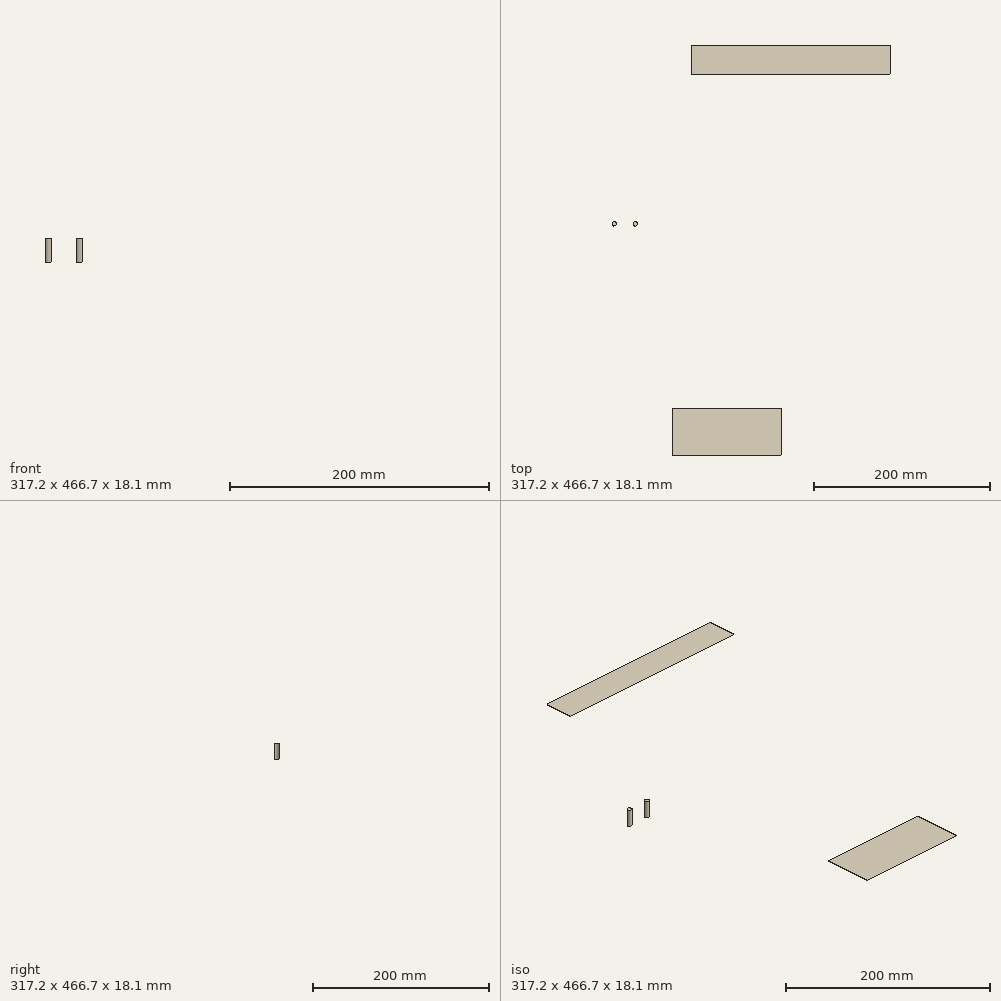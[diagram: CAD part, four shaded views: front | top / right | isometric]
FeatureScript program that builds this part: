
annotation { "Feature Type Name" : "Feature", "Feature Type Description" : "" }
export const myFeature = defineFeature(function(context is Context, id is Id, definition is map)
    precondition{}
    {
        {
            var Q0;
            Q0=qCreatedBy(makeId("Top.planeOp"),FACE);
            var sketch = newSketch(context, id + "F0", { "sketchPlane" : qUnion([Q0])});
            skLineSegment(sketch, "E0.bottom", {"start": v(0, 0) * mm, "end": v(500, 0) * mm});
            skLineSegment(sketch, "E0.top", {"start": v(0, 1000) * mm, "end": v(500, 1000) * mm});
            skLineSegment(sketch, "E0.left", {"start": v(0, 0) * mm, "end": v(0, 1000) * mm});
            skLineSegment(sketch, "E0.right", {"start": v(500, 0) * mm, "end": v(500, 1000) * mm});
            skSolve(sketch);
        }
        {
            var Q0;
            Q0=makeQuery(id+"F0.imprint","IMPRINT",FACE,{"disambiguationData":[TD([[makeQuery(id+"F0.imprint","IMPRINT",EDGE,{"derivedFrom":sQuery(id+"F0.wireOp",EDGE,"E0.bottom")}),1.0]])]});
            extrude(context, id + "F1", {"entities" : qUnion([Q0]), "depth" : 18 * mm, "offsetDistance" : 25 * mm});
        }
        {
            var Q0;
            Q0=makeQuery(id+"F1.opExtrude","CAP_FACE",FACE,{"disambiguationData":[OSD([sQuery(id+"F0.wireOp",EDGE,"E0.bottom"),sQuery(id+"F0.wireOp",EDGE,"E0.top"),sQuery(id+"F0.wireOp",EDGE,"E0.left"),sQuery(id+"F0.wireOp",EDGE,"E0.right")])],"isStart":false});
            var sketch = newSketch(context, id + "F2", { "sketchPlane" : qUnion([Q0])});
            skLineSegment(sketch, "E1", {"start": v(-62.28, 670) * mm, "end": v(483.72, 670) * mm, "construction": true});
            skLineSegment(sketch, "E2", {"start": v(93.9, 330) * mm, "end": v(390.8, 330) * mm, "construction": true});
            skSolve(sketch);
        }
        {
            var Q0;
            Q0=makeQuery(id+"F2.imprint","IMPRINT",FACE,{"disambiguationData":[TD([[makeQuery(id+"F2.imprint","IMPRINT",EDGE,{"derivedFrom":makeQuery(id+"F1.opExtrude","CAP_EDGE",EDGE,{"disambiguationData":[OSD([sQuery(id+"F0.wireOp",EDGE,"E0.bottom")])],"isStart":false})}),1.0]])]});
            var sketch = newSketch(context, id + "F3", { "sketchPlane" : qUnion([Q0])});
            skLineSegment(sketch, "E3.0", {"start": v(93.9, 330) * mm, "end": v(390.8, 330) * mm, "construction": true});
            skLineSegment(sketch, "E4.0", {"start": v(-62.28, 670) * mm, "end": v(483.72, 670) * mm, "construction": true});
            skLineSegment(sketch, "E5.bottom", {"start": v(102.01, 310) * mm, "end": v(225.73, 310) * mm});
            skLineSegment(sketch, "E5.top", {"start": v(102.01, 256.35) * mm, "end": v(225.73, 256.35) * mm});
            skLineSegment(sketch, "E5.left", {"start": v(102.01, 310) * mm, "end": v(102.01, 256.35) * mm});
            skLineSegment(sketch, "E5.right", {"start": v(225.73, 310) * mm, "end": v(225.73, 256.35) * mm});
            skLineSegment(sketch, "E6", {"start": v(123.47, 690) * mm, "end": v(317.88, 690) * mm});
            skLineSegment(sketch, "E7.bottom", {"start": v(123.47, 690) * mm, "end": v(350.68, 690) * mm});
            skLineSegment(sketch, "E7.top", {"start": v(123.47, 723.04) * mm, "end": v(350.68, 723.04) * mm});
            skLineSegment(sketch, "E7.left", {"start": v(123.47, 690) * mm, "end": v(123.47, 723.04) * mm});
            skLineSegment(sketch, "E7.right", {"start": v(350.68, 690) * mm, "end": v(350.68, 723.04) * mm});
            skSolve(sketch);
        }
        {
            var Q0;
            Q0 = qSketchRegion(id + "F3", true);
            extrude(context, id + "F4", {"entities" : qUnion([Q0]), "operationType" : NewBodyOperationType.ADD, "depth" : 0.1 * mm, "offsetDistance" : 25 * mm});
        }
        {
            var Q0;
            Q0=makeQuery(id+"F2.imprint","IMPRINT",FACE,{"disambiguationData":[TD([[makeQuery(id+"F2.imprint","IMPRINT",EDGE,{"derivedFrom":makeQuery(id+"F1.opExtrude","CAP_EDGE",EDGE,{"disambiguationData":[OSD([sQuery(id+"F0.wireOp",EDGE,"E0.bottom")])],"isStart":false})}),1.0]])]});
            var sketch = newSketch(context, id + "F5", { "sketchPlane" : qUnion([Q0])});
            skLineSegment(sketch, "E8", {"start": v(86.94, 500) * mm, "end": v(381.8, 500) * mm});
            skLineSegment(sketch, "E9.0", {"start": v(0, 0) * mm, "end": v(500, 0) * mm});
            skLineSegment(sketch, "E10.0", {"start": v(0, 1000) * mm, "end": v(500, 1000) * mm});
            skLineSegment(sketch, "E11", {"start": v(99.45, 480) * mm, "end": v(348.84, 480) * mm});
            skCircle(sketch, "E12", {"center": v(36, 480) * mm, "radius": 2.5 * mm});
            skCircle(sketch, "E13", {"center": v(60, 480) * mm, "radius": 2.5 * mm});
            skCircle(sketch, "E14.MirrorC", {"center": v(60, 520) * mm, "radius": 2.5 * mm});
            skCircle(sketch, "E15.MirrorC", {"center": v(36, 520) * mm, "radius": 2.5 * mm});
            skSolve(sketch);
        }
        {
            var Q0;
            Q0=makeQuery(id+"F5.imprint","IMPRINT",FACE,{"disambiguationData":[TD([[makeQuery(id+"F5.imprint","IMPRINT",EDGE,{"derivedFrom":sQuery(id+"F5.wireOp",EDGE,"E13")}),1.0]])]});
            var Q1;
            Q1=makeQuery(id+"F5.imprint","IMPRINT",FACE,{"disambiguationData":[TD([[makeQuery(id+"F5.imprint","IMPRINT",EDGE,{"derivedFrom":sQuery(id+"F5.wireOp",EDGE,"E12")}),1.0]])]});
            var Q2;
            Q2=makeQuery(id+"F5.imprint","IMPRINT",FACE,{"disambiguationData":[TD([[makeQuery(id+"F5.imprint","IMPRINT",EDGE,{"derivedFrom":sQuery(id+"F5.wireOp",EDGE,"E15.MirrorC")}),-1.0]])]});
            var Q3;
            Q3=makeQuery(id+"F5.imprint","IMPRINT",FACE,{"disambiguationData":[TD([[makeQuery(id+"F5.imprint","IMPRINT",EDGE,{"derivedFrom":sQuery(id+"F5.wireOp",EDGE,"E14.MirrorC")}),-1.0]])]});
            extrude(context, id + "F6", {"entities" : qUnion([Q0, Q1, Q2, Q3]), "operationType" : NewBodyOperationType.REMOVE, "endBound" : BoundingType.UP_TO_NEXT, "oppositeDirection" : true, "depth" : 25 * mm, "offsetDistance" : 25 * mm});
        }
    });
